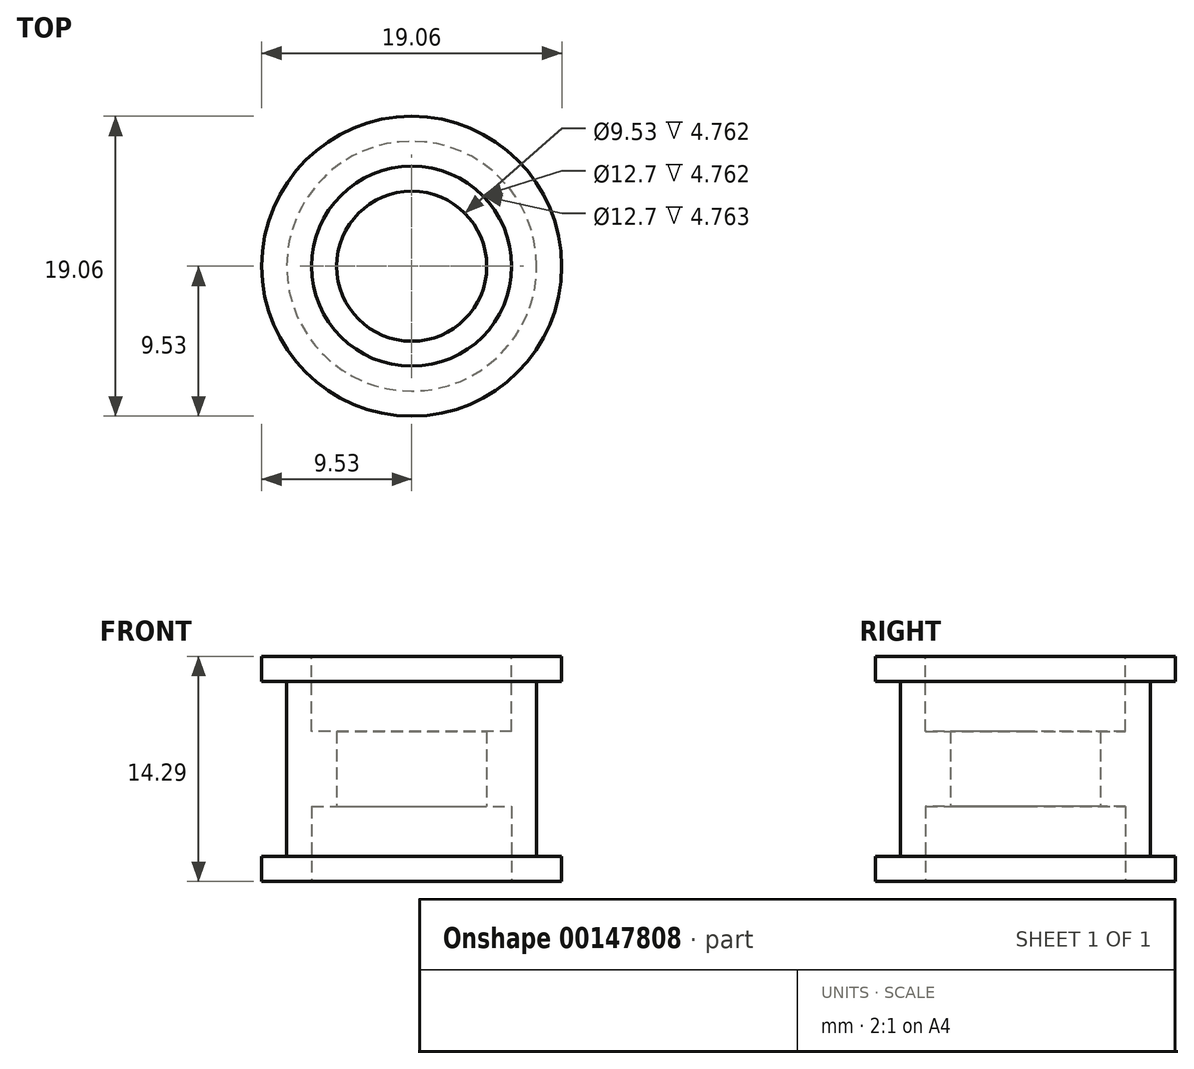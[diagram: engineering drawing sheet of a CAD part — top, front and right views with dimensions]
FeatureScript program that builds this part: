
annotation { "Feature Type Name" : "Feature", "Feature Type Description" : "" }
export const myFeature = defineFeature(function(context is Context, id is Id, definition is map)
    precondition{}
    {
        {
            var Q0;
            Q0=qCreatedBy(makeId("Top.planeOp"),FACE);
            var sketch = newSketch(context, id + "F0", { "sketchPlane" : qUnion([Q0])});
            skCircle(sketch, "E0", {"center": v(0, 0) * mm, "radius": 4.76 * mm});
            skCircle(sketch, "E1", {"center": v(0, 0) * mm, "radius": 9.53 * mm});
            skSolve(sketch);
        }
        {
            var Q0;
            Q0=qSketchRegion(id+"F0",true);
            extrude(context, id + "F1", {"entities" : qUnion([Q0]), "depth" : 14.29 * mm});
        }
        {
            var Q0;
            Q0=qCreatedBy(makeId("Front.planeOp"),FACE);
            var sketch = newSketch(context, id + "F2", { "sketchPlane" : qUnion([Q0])});
            skLineSegment(sketch, "E2", {"start": v(0, 14.29) * mm, "end": v(0, 0) * mm, "construction": true});
            skLineSegment(sketch, "E3", {"start": v(0, 7.14) * mm, "end": v(-7.94, 7.14) * mm, "construction": true});
            skLineSegment(sketch, "E4.bottom", {"start": v(-9.53, 12.7) * mm, "end": v(-7.94, 12.7) * mm});
            skLineSegment(sketch, "E4.top", {"start": v(-9.52, 1.59) * mm, "end": v(-7.94, 1.59) * mm});
            skLineSegment(sketch, "E4.left", {"start": v(-9.53, 12.7) * mm, "end": v(-9.53, 1.59) * mm});
            skLineSegment(sketch, "E4.right", {"start": v(-7.94, 12.7) * mm, "end": v(-7.94, 1.59) * mm});
            skSolve(sketch);
        }
        {
            var Q0;
            Q0=qSketchRegion(id+"F2",true);
            var Q1;
            Q1=makeQuery(id+"F1.opExtrude","SWEPT_FACE",FACE,{"disambiguationData":[OSD([sQuery(id+"F0.wireOp",EDGE,"E1")])]});
            revolve(context, id + "F3", {"operationType" : NewBodyOperationType.REMOVE, "entities" : qUnion([Q0]), "axis" : qUnion([Q1]), "revolveType" : RevolveType.FULL, "oppositeDirection" : true});
        }
        {
            var Q0;
            Q0=makeQuery(id+"F1.opExtrude","CAP_FACE",FACE,{"disambiguationData":[OSD([sQuery(id+"F0.wireOp",EDGE,"E0"),sQuery(id+"F0.wireOp",EDGE,"E1")])],"isStart":false});
            var sketch = newSketch(context, id + "F4", { "sketchPlane" : qUnion([Q0])});
            skCircle(sketch, "E5", {"center": v(0, 0) * mm, "radius": 6.35 * mm});
            skSolve(sketch);
        }
        {
            var Q0;
            Q0=qSketchRegion(id+"F4",true);
            extrude(context, id + "F5", {"entities" : qUnion([Q0]), "operationType" : NewBodyOperationType.REMOVE, "oppositeDirection" : true, "depth" : 4.76 * mm});
        }
        {
            var Q0;
            Q0=makeQuery(id+"F1.opExtrude","CAP_FACE",FACE,{"disambiguationData":[OSD([sQuery(id+"F0.wireOp",EDGE,"E0"),sQuery(id+"F0.wireOp",EDGE,"E1")])],"isStart":true});
            var sketch = newSketch(context, id + "F6", { "sketchPlane" : qUnion([Q0])});
            skCircle(sketch, "E6", {"center": v(0, 0) * mm, "radius": 6.35 * mm});
            skSolve(sketch);
        }
        {
            var Q0;
            Q0=qSketchRegion(id+"F6",true);
            extrude(context, id + "F7", {"entities" : qUnion([Q0]), "operationType" : NewBodyOperationType.REMOVE, "oppositeDirection" : true, "depth" : 4.76 * mm});
        }
    });
